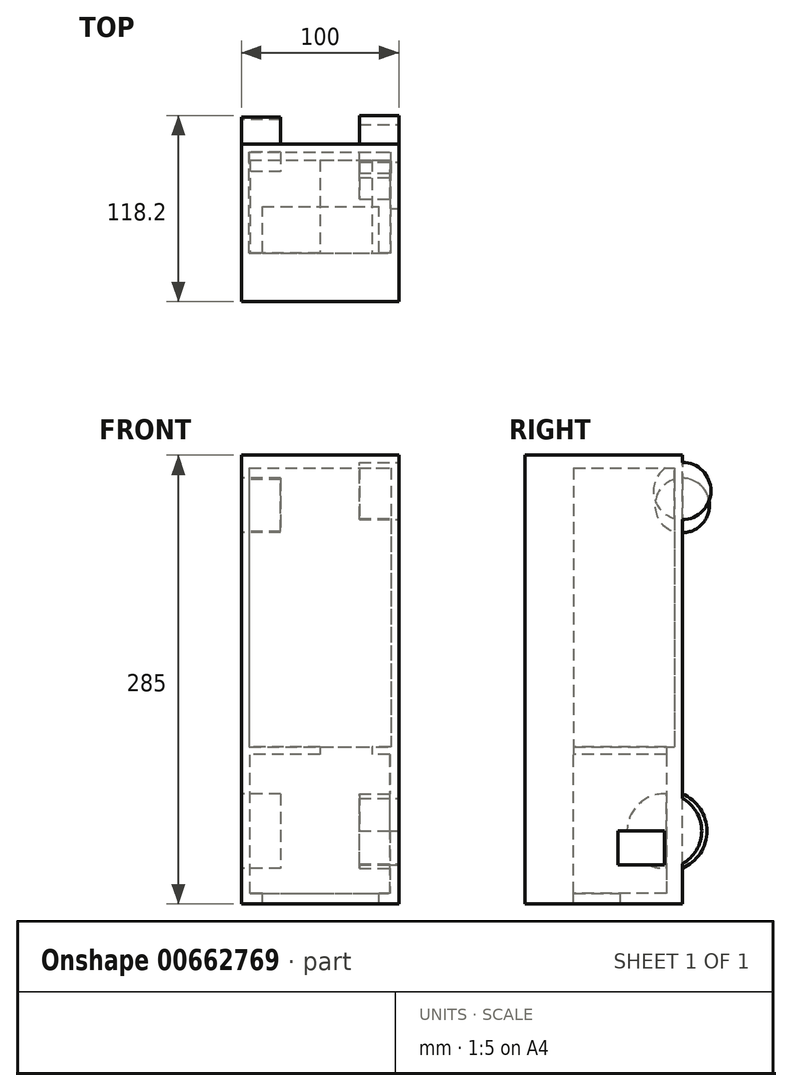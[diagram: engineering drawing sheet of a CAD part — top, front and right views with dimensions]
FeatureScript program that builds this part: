
annotation { "Feature Type Name" : "Feature", "Feature Type Description" : "" }
export const myFeature = defineFeature(function(context is Context, id is Id, definition is map)
    precondition{}
    {
        {
            var Q0;
            Q0=qCreatedBy(makeId("Front.planeOp"),FACE);
            var sketch = newSketch(context, id + "F0", { "sketchPlane" : qUnion([Q0])});
            skLineSegment(sketch, "E0.bottom", {"start": v(-56.52, 53.75) * mm, "end": v(43.48, 53.75) * mm});
            skLineSegment(sketch, "E0.top", {"start": v(-56.52, -46.25) * mm, "end": v(43.48, -46.25) * mm});
            skLineSegment(sketch, "E0.left", {"start": v(-56.52, 53.75) * mm, "end": v(-56.52, -46.25) * mm});
            skLineSegment(sketch, "E0.right", {"start": v(43.48, 53.75) * mm, "end": v(43.48, -46.25) * mm});
            skSolve(sketch);
        }
        {
            var Q0;
            Q0=makeQuery(id+"F0.imprint","IMPRINT",FACE,{"disambiguationData":[TD([[makeQuery(id+"F0.imprint","IMPRINT",EDGE,{"derivedFrom":sQuery(id+"F0.wireOp",EDGE,"E0.bottom")}),-1.0]])]});
            extrude(context, id + "F1", {"entities" : qUnion([Q0]), "depth" : 100 * mm, "offsetDistance" : 25 * mm});
        }
        {
            var Q0;
            Q0=makeQuery(id+"F1.opExtrude","CAP_FACE",FACE,{"disambiguationData":[OSD([sQuery(id+"F0.wireOp",EDGE,"E0.bottom"),sQuery(id+"F0.wireOp",EDGE,"E0.top"),sQuery(id+"F0.wireOp",EDGE,"E0.left"),sQuery(id+"F0.wireOp",EDGE,"E0.right")])],"isStart":false});
            var sketch = newSketch(context, id + "F2", { "sketchPlane" : qUnion([Q0])});
            skLineSegment(sketch, "E1.bottom", {"start": v(-51.13, 48.55) * mm, "end": v(37.8, 48.55) * mm});
            skLineSegment(sketch, "E1.top", {"start": v(-51.13, -39.7) * mm, "end": v(37.8, -39.7) * mm});
            skLineSegment(sketch, "E1.left", {"start": v(-51.13, 48.55) * mm, "end": v(-51.13, -39.7) * mm});
            skLineSegment(sketch, "E1.right", {"start": v(37.8, 48.55) * mm, "end": v(37.8, -39.7) * mm});
            skSolve(sketch);
        }
        {
            var Q0;
            Q0 = qSketchRegion(id + "F2", true);
            extrude(context, id + "F3", {"entities" : qUnion([Q0]), "operationType" : NewBodyOperationType.REMOVE, "oppositeDirection" : true, "depth" : 90 * mm, "offsetDistance" : 25 * mm});
        }
        {
            var Q0;
            Q0=makeQuery(id+"F1.opExtrude","SWEPT_FACE",FACE,{"disambiguationData":[OSD([sQuery(id+"F0.wireOp",EDGE,"E0.bottom")])]});
            var sketch = newSketch(context, id + "F4", { "sketchPlane" : qUnion([Q0])});
            skLineSegment(sketch, "E2", {"start": v(-39.27, -27.85) * mm, "end": v(-25.93, -78.99) * mm});
            skLineSegment(sketch, "E3", {"start": v(-25.93, -78.99) * mm, "end": v(21.09, -66.72) * mm});
            skLineSegment(sketch, "E4", {"start": v(19.65, -61.2) * mm, "end": v(32.99, -78.99) * mm});
            skLineSegment(sketch, "E5", {"start": v(32.99, -78.99) * mm, "end": v(43.48, -33.41) * mm});
            skLineSegment(sketch, "E6", {"start": v(43.48, -33.41) * mm, "end": v(-39.27, -27.85) * mm});
            skSolve(sketch);
        }
        {
            var Q0;
            Q0 = qSketchRegion(id + "F4", true);
            var Q1;
            {var subQ0=sQuery(id+"F0.wireOp",EDGE,"E0.bottom");var subQ1=makeQuery(id+"F1.opExtrude","CAP_EDGE",EDGE,{"disambiguationData":[OSD([subQ0])],"isStart":true});Q1=makeQuery(id+"F4.imprint","IMPRINT",FACE,{"disambiguationData":[TD([[makeQuery(id+"F4.imprint","IMPRINT",EDGE,{"derivedFrom":subQ1}),-1.0]])]});}
            extrude(context, id + "F5", {"entities" : qUnion([Q0, Q1]), "operationType" : NewBodyOperationType.ADD, "depth" : 185 * mm, "offsetDistance" : 25 * mm});
        }
        {
            var Q0;
            {var subQ0=sQuery(id+"F0.wireOp",EDGE,"E0.bottom");Q0=makeQuery(id+"F5.boolean.opBoolean","MERGE",FACE,{"derivedFrom":[makeQuery(id+"F1.opExtrude","CAP_FACE",FACE,{"disambiguationData":[OSD([subQ0,sQuery(id+"F0.wireOp",EDGE,"E0.top"),sQuery(id+"F0.wireOp",EDGE,"E0.left"),sQuery(id+"F0.wireOp",EDGE,"E0.right")])],"isStart":false}),makeQuery(id+"F5.opExtrude","SWEPT_FACE",FACE,{"disambiguationData":[OSD([subQ0]),TDD([makeQuery(id+"F4.imprint","IMPRINT",EDGE,{"derivedFrom":makeQuery(id+"F1.opExtrude","CAP_EDGE",EDGE,{"disambiguationData":[OSD([subQ0])],"isStart":false})})])]})]});}
            var Q1;
            Q1=makeQuery(id+"F5.opExtrude","CAP_FACE",FACE,{"disambiguationData":[OSD([sQuery(id+"F0.wireOp",EDGE,"E0.bottom"),sQuery(id+"F0.wireOp",EDGE,"E0.left"),sQuery(id+"F0.wireOp",EDGE,"E0.right")])],"isStart":false});
            shell(context, id + "F6", {"entities" : qUnion([Q0, Q1]), "thickness" : 5 * mm});
        }
        {
            var Q0;
            Q0=makeQuery(id+"F5.opExtrude","CAP_FACE",FACE,{"disambiguationData":[OSD([sQuery(id+"F0.wireOp",EDGE,"E0.bottom"),sQuery(id+"F0.wireOp",EDGE,"E0.left"),sQuery(id+"F0.wireOp",EDGE,"E0.right")])],"isStart":false});
            var sketch = newSketch(context, id + "F7", { "sketchPlane" : qUnion([Q0])});
            skLineSegment(sketch, "E7.bottom", {"start": v(-51.52, -5) * mm, "end": v(38.48, -5) * mm});
            skLineSegment(sketch, "E7.top", {"start": v(-51.52, -100) * mm, "end": v(38.48, -100) * mm});
            skLineSegment(sketch, "E7.left", {"start": v(-51.52, -5) * mm, "end": v(-51.52, -100) * mm});
            skLineSegment(sketch, "E7.right", {"start": v(38.48, -5) * mm, "end": v(38.48, -100) * mm});
            skSolve(sketch);
        }
        {
            var Q0;
            Q0=makeQuery(id+"F7.imprint","IMPRINT",FACE,{"disambiguationData":[TD([[makeQuery(id+"F7.imprint","IMPRINT",EDGE,{"derivedFrom":sQuery(id+"F7.wireOp",EDGE,"E7.bottom")}),-1.0]])]});
            extrude(context, id + "F8", {"entities" : qUnion([Q0]), "operationType" : NewBodyOperationType.ADD, "oppositeDirection" : true, "depth" : 8 * mm, "offsetDistance" : 25 * mm});
        }
        {
            var Q0;
            {var subQ0=sQuery(id+"F0.wireOp",EDGE,"E0.left");Q0=makeQuery(id+"F5.boolean.opBoolean","MERGE",FACE,{"derivedFrom":[makeQuery(id+"F1.opExtrude","SWEPT_FACE",FACE,{"disambiguationData":[OSD([subQ0])]}),makeQuery(id+"F5.opExtrude","SWEPT_FACE",FACE,{"disambiguationData":[OSD([sQuery(id+"F0.wireOp",EDGE,"E0.bottom"),subQ0])]})]});}
            var sketch = newSketch(context, id + "F9", { "sketchPlane" : qUnion([Q0])});
            skCircle(sketch, "E8", {"center": v(0, 206.84) * mm, "radius": 17.33 * mm});
            skCircle(sketch, "E9", {"center": v(9.93, 0) * mm, "radius": 25.66 * mm});
            skSolve(sketch);
        }
        {
            var Q0;
            {var subQ0=sQuery(id+"F9.wireOp",EDGE,"E8");var subQ1=sQuery(id+"F0.wireOp",EDGE,"E0.bottom");var subQ2=sQuery(id+"F0.wireOp",EDGE,"E0.left");var subQ3=makeQuery(id+"F5.boolean.opBoolean","MERGE",EDGE,{"derivedFrom":[makeQuery(id+"F1.opExtrude","CAP_EDGE",EDGE,{"disambiguationData":[OSD([subQ2])],"isStart":true}),makeQuery(id+"F5.opExtrude","SWEPT_EDGE",EDGE,{"disambiguationData":[OSD([subQ1,subQ2]),TDD([makeQuery(id+"F4.imprint","INTERSECT",VERTEX,{"derivedFrom":[makeQuery(id+"F1.opExtrude","SWEPT_EDGE",EDGE,{"disambiguationData":[OSD([subQ1,subQ2])]}),makeQuery(id+"F1.opExtrude","CAP_EDGE",EDGE,{"disambiguationData":[OSD([subQ1])],"isStart":true})]})])]})]});var subQ4=makeQuery(id+"F9.imprint","INTERSECT",VERTEX,{"disambiguationData":[OD(0.0)],"derivedFrom":[subQ3,subQ0]});Q0=makeQuery(id+"F9.imprint","IMPRINT",FACE,{"disambiguationData":[TD([[makeQuery(id+"F9.imprint","IMPRINT",EDGE,{"disambiguationData":[TD([[subQ4,-1.0]])],"derivedFrom":subQ0}),1.0]])]});}
            var Q1;
            {var subQ0=sQuery(id+"F9.wireOp",EDGE,"E9");var subQ1=sQuery(id+"F0.wireOp",EDGE,"E0.bottom");var subQ2=sQuery(id+"F0.wireOp",EDGE,"E0.left");var subQ3=makeQuery(id+"F5.boolean.opBoolean","MERGE",EDGE,{"derivedFrom":[makeQuery(id+"F1.opExtrude","CAP_EDGE",EDGE,{"disambiguationData":[OSD([subQ2])],"isStart":true}),makeQuery(id+"F5.opExtrude","SWEPT_EDGE",EDGE,{"disambiguationData":[OSD([subQ1,subQ2]),TDD([makeQuery(id+"F4.imprint","INTERSECT",VERTEX,{"derivedFrom":[makeQuery(id+"F1.opExtrude","SWEPT_EDGE",EDGE,{"disambiguationData":[OSD([subQ1,subQ2])]}),makeQuery(id+"F1.opExtrude","CAP_EDGE",EDGE,{"disambiguationData":[OSD([subQ1])],"isStart":true})]})])]})]});var subQ4=makeQuery(id+"F9.imprint","INTERSECT",VERTEX,{"disambiguationData":[OD(0.0)],"derivedFrom":[subQ3,subQ0]});Q1=makeQuery(id+"F9.imprint","IMPRINT",FACE,{"disambiguationData":[TD([[makeQuery(id+"F9.imprint","IMPRINT",EDGE,{"disambiguationData":[TD([[subQ4,1.0]])],"derivedFrom":subQ0}),1.0]])]});}
            var Q2;
            {var subQ0=sQuery(id+"F9.wireOp",EDGE,"E8");var subQ1=sQuery(id+"F0.wireOp",EDGE,"E0.bottom");var subQ2=sQuery(id+"F0.wireOp",EDGE,"E0.left");var subQ3=makeQuery(id+"F5.boolean.opBoolean","MERGE",EDGE,{"derivedFrom":[makeQuery(id+"F1.opExtrude","CAP_EDGE",EDGE,{"disambiguationData":[OSD([subQ2])],"isStart":true}),makeQuery(id+"F5.opExtrude","SWEPT_EDGE",EDGE,{"disambiguationData":[OSD([subQ1,subQ2]),TDD([makeQuery(id+"F4.imprint","INTERSECT",VERTEX,{"derivedFrom":[makeQuery(id+"F1.opExtrude","SWEPT_EDGE",EDGE,{"disambiguationData":[OSD([subQ1,subQ2])]}),makeQuery(id+"F1.opExtrude","CAP_EDGE",EDGE,{"disambiguationData":[OSD([subQ1])],"isStart":true})]})])]})]});var subQ4=makeQuery(id+"F9.imprint","INTERSECT",VERTEX,{"disambiguationData":[OD(0.0)],"derivedFrom":[subQ3,subQ0]});Q2=makeQuery(id+"F9.imprint","IMPRINT",FACE,{"disambiguationData":[TD([[makeQuery(id+"F9.imprint","IMPRINT",EDGE,{"disambiguationData":[TD([[subQ4,1.0]])],"derivedFrom":subQ0}),1.0]])]});}
            extrude(context, id + "F10", {"entities" : qUnion([Q0, Q1, Q2]), "operationType" : NewBodyOperationType.ADD, "oppositeDirection" : true, "depth" : 25 * mm, "offsetDistance" : 25 * mm});
        }
        {
            var Q0;
            {var subQ0=sQuery(id+"F0.wireOp",EDGE,"E0.right");Q0=makeQuery(id+"F5.boolean.opBoolean","MERGE",FACE,{"derivedFrom":[makeQuery(id+"F1.opExtrude","SWEPT_FACE",FACE,{"disambiguationData":[OSD([subQ0])]}),makeQuery(id+"F5.opExtrude","SWEPT_FACE",FACE,{"disambiguationData":[OSD([sQuery(id+"F0.wireOp",EDGE,"E0.bottom"),subQ0])]})]});}
            var sketch = newSketch(context, id + "F11", { "sketchPlane" : qUnion([Q0])});
            skCircle(sketch, "E10", {"center": v(-11.27, 0) * mm, "radius": 23.68 * mm});
            skCircle(sketch, "E11", {"center": v(0, 216.04) * mm, "radius": 18.2 * mm});
            skSolve(sketch);
        }
        {
            var Q0;
            Q0 = qSketchRegion(id + "F11", true);
            extrude(context, id + "F12", {"entities" : qUnion([Q0]), "operationType" : NewBodyOperationType.ADD, "oppositeDirection" : true, "depth" : 25 * mm, "offsetDistance" : 25 * mm});
        }
        {
            var Q0;
            Q0=makeQuery(id+"F1.opExtrude","SWEPT_FACE",FACE,{"disambiguationData":[OSD([sQuery(id+"F0.wireOp",EDGE,"E0.top")])]});
            var sketch = newSketch(context, id + "F13", { "sketchPlane" : qUnion([Q0])});
            skLineSegment(sketch, "E12.bottom", {"start": v(-43.13, 79.75) * mm, "end": v(30.9, 79.75) * mm});
            skLineSegment(sketch, "E12.top", {"start": v(-43.13, 39.43) * mm, "end": v(30.9, 39.43) * mm});
            skLineSegment(sketch, "E12.left", {"start": v(-43.13, 79.75) * mm, "end": v(-43.13, 39.43) * mm});
            skLineSegment(sketch, "E12.right", {"start": v(30.9, 79.75) * mm, "end": v(30.9, 39.43) * mm});
            skSolve(sketch);
        }
        {
            var Q0;
            Q0=makeQuery(id+"F13.imprint","IMPRINT",FACE,{"disambiguationData":[TD([[makeQuery(id+"F13.imprint","IMPRINT",EDGE,{"derivedFrom":sQuery(id+"F13.wireOp",EDGE,"E12.bottom")}),-1.0]])]});
            extrude(context, id + "F14", {"entities" : qUnion([Q0]), "operationType" : NewBodyOperationType.REMOVE, "oppositeDirection" : true, "depth" : 9 * mm, "offsetDistance" : 25 * mm});
        }
        {
            var Q0;
            Q0=makeQuery(id+"F3.boolean.opBoolean","COPY",FACE,{"derivedFrom":makeQuery(id+"F3.opExtrude","SWEPT_FACE",FACE,{"disambiguationData":[OSD([sQuery(id+"F2.wireOp",EDGE,"E1.bottom")])]})});
            var sketch = newSketch(context, id + "F15", { "sketchPlane" : qUnion([Q0])});
            skLineSegment(sketch, "E13.bottom", {"start": v(-6.67, 10) * mm, "end": v(26.5, 10) * mm});
            skLineSegment(sketch, "E13.top", {"start": v(-6.67, 73.8) * mm, "end": v(26.5, 73.8) * mm});
            skLineSegment(sketch, "E13.left", {"start": v(-6.67, 10) * mm, "end": v(-6.67, 73.8) * mm});
            skLineSegment(sketch, "E13.right", {"start": v(26.5, 10) * mm, "end": v(26.5, 73.8) * mm});
            skSolve(sketch);
        }
        {
            var Q0;
            Q0=makeQuery(id+"F15.imprint","IMPRINT",FACE,{"disambiguationData":[TD([[makeQuery(id+"F15.imprint","IMPRINT",EDGE,{"derivedFrom":sQuery(id+"F15.wireOp",EDGE,"E13.bottom")}),1.0]])]});
            extrude(context, id + "F16", {"entities" : qUnion([Q0]), "operationType" : NewBodyOperationType.REMOVE, "oppositeDirection" : true, "depth" : 25 * mm, "offsetDistance" : 25 * mm});
        }
        {
            var Q0;
            {var subQ0=sQuery(id+"F0.wireOp",EDGE,"E0.bottom");Q0=makeQuery(id+"F8.boolean.opBoolean","MERGE",FACE,{"derivedFrom":[makeQuery(id+"F5.boolean.opBoolean","MERGE",FACE,{"derivedFrom":[makeQuery(id+"F1.opExtrude","CAP_FACE",FACE,{"disambiguationData":[OSD([subQ0,sQuery(id+"F0.wireOp",EDGE,"E0.top"),sQuery(id+"F0.wireOp",EDGE,"E0.left"),sQuery(id+"F0.wireOp",EDGE,"E0.right")])],"isStart":false}),makeQuery(id+"F5.opExtrude","SWEPT_FACE",FACE,{"disambiguationData":[OSD([subQ0]),TDD([makeQuery(id+"F4.imprint","IMPRINT",EDGE,{"derivedFrom":makeQuery(id+"F1.opExtrude","CAP_EDGE",EDGE,{"disambiguationData":[OSD([subQ0])],"isStart":false})})])]})]}),makeQuery(id+"F8.opExtrude","SWEPT_FACE",FACE,{"disambiguationData":[OSD([sQuery(id+"F7.wireOp",EDGE,"E7.top")])]})]});}
            var sketch = newSketch(context, id + "F17", { "sketchPlane" : qUnion([Q0])});
            skLineSegment(sketch, "E14.bottom", {"start": v(-56.52, -46.25) * mm, "end": v(38.48, -46.25) * mm});
            skLineSegment(sketch, "E14.top", {"start": v(-56.52, 230.75) * mm, "end": v(38.48, 230.75) * mm});
            skLineSegment(sketch, "E14.left", {"start": v(-56.52, -46.25) * mm, "end": v(-56.52, 230.75) * mm});
            skLineSegment(sketch, "E14.right", {"start": v(38.48, -46.25) * mm, "end": v(38.48, 230.75) * mm});
            skSolve(sketch);
        }
        {
            var Q0;
            Q0 = qSketchRegion(id + "F17", true);
            extrude(context, id + "F18", {"entities" : qUnion([Q0]), "operationType" : NewBodyOperationType.ADD, "oppositeDirection" : true, "depth" : 31 * mm, "offsetDistance" : 25 * mm});
        }
        {
            var Q0;
            {var subQ0=sQuery(id+"F0.wireOp",EDGE,"E0.right");Q0=makeQuery(id+"F12.boolean.opBoolean","MERGE",FACE,{"derivedFrom":[makeQuery(id+"F5.boolean.opBoolean","MERGE",FACE,{"derivedFrom":[makeQuery(id+"F1.opExtrude","SWEPT_FACE",FACE,{"disambiguationData":[OSD([subQ0])]}),makeQuery(id+"F5.opExtrude","SWEPT_FACE",FACE,{"disambiguationData":[OSD([sQuery(id+"F0.wireOp",EDGE,"E0.bottom"),subQ0])]})]}),makeQuery(id+"F12.opExtrude","CAP_FACE",FACE,{"disambiguationData":[OSD([sQuery(id+"F11.wireOp",EDGE,"E10")])],"isStart":true}),makeQuery(id+"F12.opExtrude","CAP_FACE",FACE,{"disambiguationData":[OSD([sQuery(id+"F11.wireOp",EDGE,"E11")])],"isStart":true})]});}
            var sketch = newSketch(context, id + "F19", { "sketchPlane" : qUnion([Q0])});
            skLineSegment(sketch, "E15.bottom", {"start": v(-40.82, -21.47) * mm, "end": v(-11.27, -21.47) * mm});
            skLineSegment(sketch, "E15.top", {"start": v(-40.82, 0) * mm, "end": v(-11.27, 0) * mm});
            skLineSegment(sketch, "E15.left", {"start": v(-40.82, -21.47) * mm, "end": v(-40.82, 0) * mm});
            skLineSegment(sketch, "E15.right", {"start": v(-11.27, -21.47) * mm, "end": v(-11.27, 0) * mm});
            skSolve(sketch);
        }
        {
            var Q0;
            Q0 = qSketchRegion(id + "F19", true);
            extrude(context, id + "F20", {"entities" : qUnion([Q0]), "operationType" : NewBodyOperationType.REMOVE, "oppositeDirection" : true, "depth" : 25 * mm, "offsetDistance" : 25 * mm});
        }
    });
